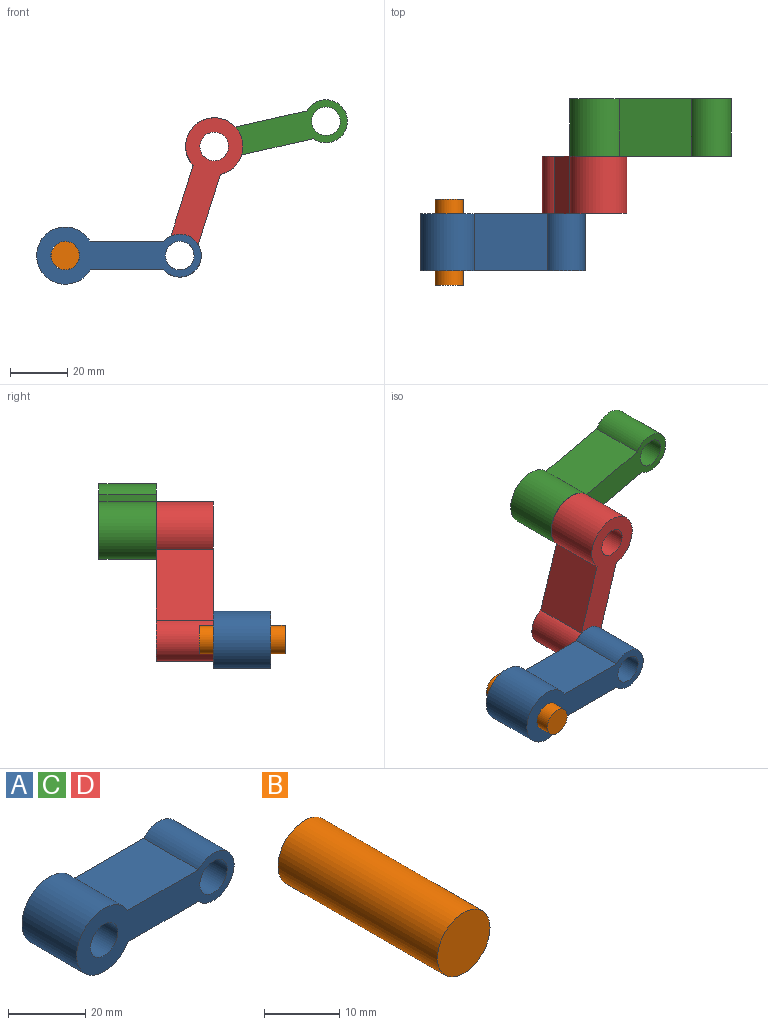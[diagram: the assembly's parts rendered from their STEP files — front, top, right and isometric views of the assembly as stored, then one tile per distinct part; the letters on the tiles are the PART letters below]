
ASSEMBLY  parts=4 mates=3
PART A: 8 faces, bbox 57.5x20x20 mm
  f0: plane 25.75x20mm, normal (0,0,1), area 515mm2, adj f1,f4,f6,f7
  f1: cylinder r=10mm len=20mm, axis (0,1,0), area 1047.2mm2, adj f0,f2,f6,f7
  f2: plane 25.75x20mm, normal (0,0,-1), area 515mm2, adj f1,f4,f6,f7
  f3: cylinder r=5mm len=20mm, axis (0,1,0), area 628.3mm2, adj f6,f7
  f4: cylinder r=7.5mm len=20mm, axis (0,1,0), area 723.6mm2, adj f0,f2,f6,f7
  f5: cylinder r=5mm len=20mm, axis (0,1,0), area 628.3mm2, adj f6,f7
  f6: plane 57.5x20mm, normal (0,-1,0), area 569.1mm2, adj f0,f1,f2,f3,f4,f5
  f7: plane 57.5x20mm, normal (0,1,0), area 569.1mm2, adj f0,f1,f2,f3,f4,f5
PART B: 3 faces, bbox 9.9x30x9.9 mm
  f0: cylinder r=4.95mm len=30mm, axis (0,1,0), area 933.1mm2, adj f1,f2
  f1: plane 9.9x9.9mm, normal (0,-1,0), area 77mm2, adj f0
  f2: plane 9.9x9.9mm, normal (0,1,0), area 77mm2, adj f0
PART C: same geometry as A
PART D: same geometry as A
PLACE A t=(-15.14,-23.31,-35.54)mm
PLACE B t=(-15.14,-23.31,-35.54)mm fixed
PLACE C rot(axis=(0,-1,0),12.7deg) t=(36.91,16.69,2.6)mm
PLACE D rot(axis=(0,1,0),107.5deg) t=(36.91,-3.31,2.6)mm
MATE revolute D.f3 <-> A.f3  axis (0,1,0) through (24.86,-13.31,-35.54)mm
MATE pin_slot A.f1 <-> B.f0  axis (0,1,0) through (-15.14,-23.31,-35.54)mm
MATE revolute C.f1 <-> D.f1  axis (0,-1,0) through (36.91,6.69,2.6)mm
